# Revit family: 1802a_lvseries
name_source: partatom
category: Communication Devices
units: mm (PartAtom-declared; Revit-internal decimal feet)

## family parameters
Cut with Voids When Loaded = No
Host = Face
Maintain Annotation Orientation = No
OmniClass Number = 23.85.80.11.27
OmniClass Title = Lighting Controls
Part Type = Normal
Room Calculation Point = No
Round Connector Dimension = Use Diameter
Shared = Yes

## types (2) — shared parameters
Assembly Code = D5090
Black = Paint - Carbon Black
Default Elevation = 48 "
Description = Our Low Voltage Wall Switches are designed for virtually any
area. The soft contours of its architecturally-pleasing design fit
easily into any décor. Momentary version switches are available
and feature multiple button configurations making them the
perfect switch solution for low voltage occupancy sensors,
daylighting controls and networked lighting control panels.
Features = Attractive, architecturally pleasing design
• Momentary or latching button action
• 1-4 buttons with or without LED
• Mounts to standard single-gang box
• California Title 24 compliant
• Five-year limited warranty
• Low voltage device: 24VDC
Height = 4.5 "
Manufacturer = NX Lighting Controls
Model = Low Voltage Switches
Type Comments = Low Voltage Switches
URL = https://www.currentlighting.com
Warranty = 5-Years Warranty
White = Paint -  Matte White
Width = 2.75 "

## per-type parameters (varying)
| type | LED |
| LVSM1NP | No |
| LVSM1PL | Yes |

## geometry (parser evidence)
native form markers: Sweep x3
no freeform markers — native parametric forms only
